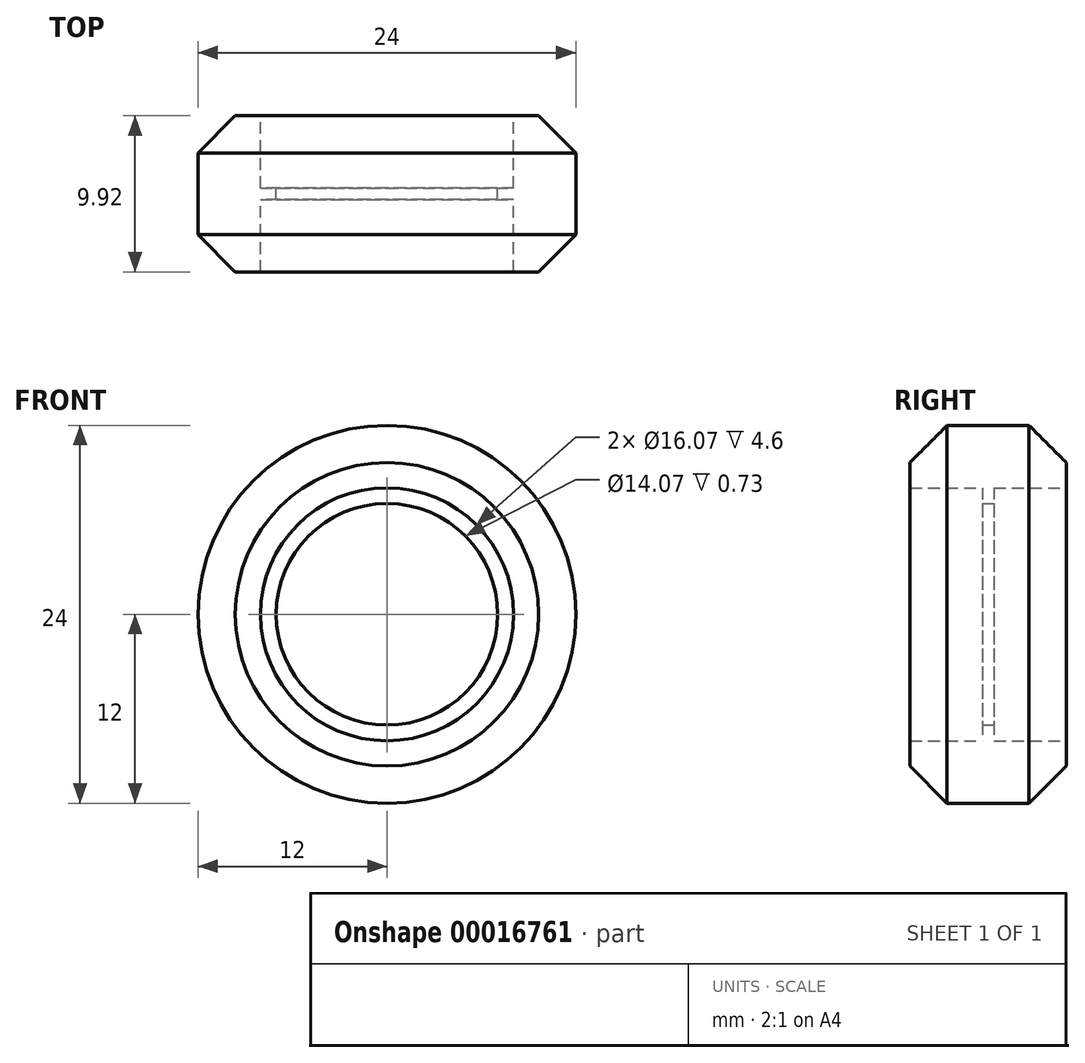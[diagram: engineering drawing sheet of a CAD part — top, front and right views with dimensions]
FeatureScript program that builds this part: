
annotation { "Feature Type Name" : "Feature", "Feature Type Description" : "" }
export const myFeature = defineFeature(function(context is Context, id is Id, definition is map)
    precondition{}
    {
        {
            var Q0;
            Q0=qCreatedBy(makeId("Right.planeOp"),FACE);
            var sketch = newSketch(context, id + "F0", { "sketchPlane" : qUnion([Q0])});
            skLineSegment(sketch, "E0", {"start": v(0.36, 7.04) * mm, "end": v(0.36, 8.04) * mm});
            skLineSegment(sketch, "E1", {"start": v(0.36, 8.04) * mm, "end": v(4.96, 8.04) * mm});
            skLineSegment(sketch, "E2", {"start": v(4.96, 8.04) * mm, "end": v(4.96, 9.64) * mm});
            skLineSegment(sketch, "E3", {"start": v(4.96, 9.64) * mm, "end": v(2.6, 12) * mm});
            skLineSegment(sketch, "E4.MirrorCS", {"start": v(-0.36, 7.04) * mm, "end": v(-0.36, 8.04) * mm});
            skLineSegment(sketch, "E5.MirrorCS", {"start": v(-4.96, 9.64) * mm, "end": v(-2.6, 12) * mm});
            skLineSegment(sketch, "E6.MirrorCS", {"start": v(-0.36, 8.04) * mm, "end": v(-4.96, 8.04) * mm});
            skLineSegment(sketch, "E7.MirrorCS", {"start": v(-4.96, 8.04) * mm, "end": v(-4.96, 9.64) * mm});
            skLineSegment(sketch, "E8", {"start": v(2.41, 0) * mm, "end": v(-2.28, 0) * mm, "construction": true});
            skLineSegment(sketch, "E9", {"start": v(0, 12) * mm, "end": v(0, 0) * mm, "construction": true});
            skLineSegment(sketch, "E10", {"start": v(-4.96, 9.64) * mm, "end": v(-4.96, 12) * mm, "construction": true});
            skLineSegment(sketch, "E11", {"start": v(-4.96, 12) * mm, "end": v(-2.6, 12) * mm, "construction": true});
            skPoint(sketch, "E12.MirrorCS.end.orphan", {"position": v(0, 12) * mm});
            skPoint(sketch, "E13.MirrorCS.start.orphan", {"position": v(0, 7.04) * mm});
            skLineSegment(sketch, "E14", {"start": v(-2.6, 12) * mm, "end": v(2.6, 12) * mm});
            skLineSegment(sketch, "E15", {"start": v(-0.36, 7.04) * mm, "end": v(0.36, 7.04) * mm});
            skSolve(sketch);
        }
        {
            var Q0;
            Q0=qSketchRegion(id+"F0",true);
            var Q1;
            Q1=sQuery(id+"F0.wireOp",EDGE,"E8");
            revolve(context, id + "F1", {"entities" : qUnion([Q0]), "axis" : qUnion([Q1]), "revolveType" : RevolveType.FULL});
        }
    });
